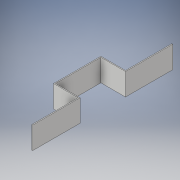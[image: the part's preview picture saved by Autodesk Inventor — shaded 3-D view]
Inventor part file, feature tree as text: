
AUTODESK INVENTOR PART (.ipt)
format: ipt  version: 2019 (Build 230136000, 136)  size: 112,640 bytes
history: native  units: mm
features: other x1, extrude x1, sketch x1
ambient origin geometry x8: Origin, YZ Plane, XZ Plane, XY Plane, X Axis, Y Axis, Z Axis, Center Point
bodies: Body1 (feature_tree)
feature tree (3):
  other  "ソリッド1"
  extrude  "押し出し1"  Depth=150.0mm
  sketch  "スケッチ1"
